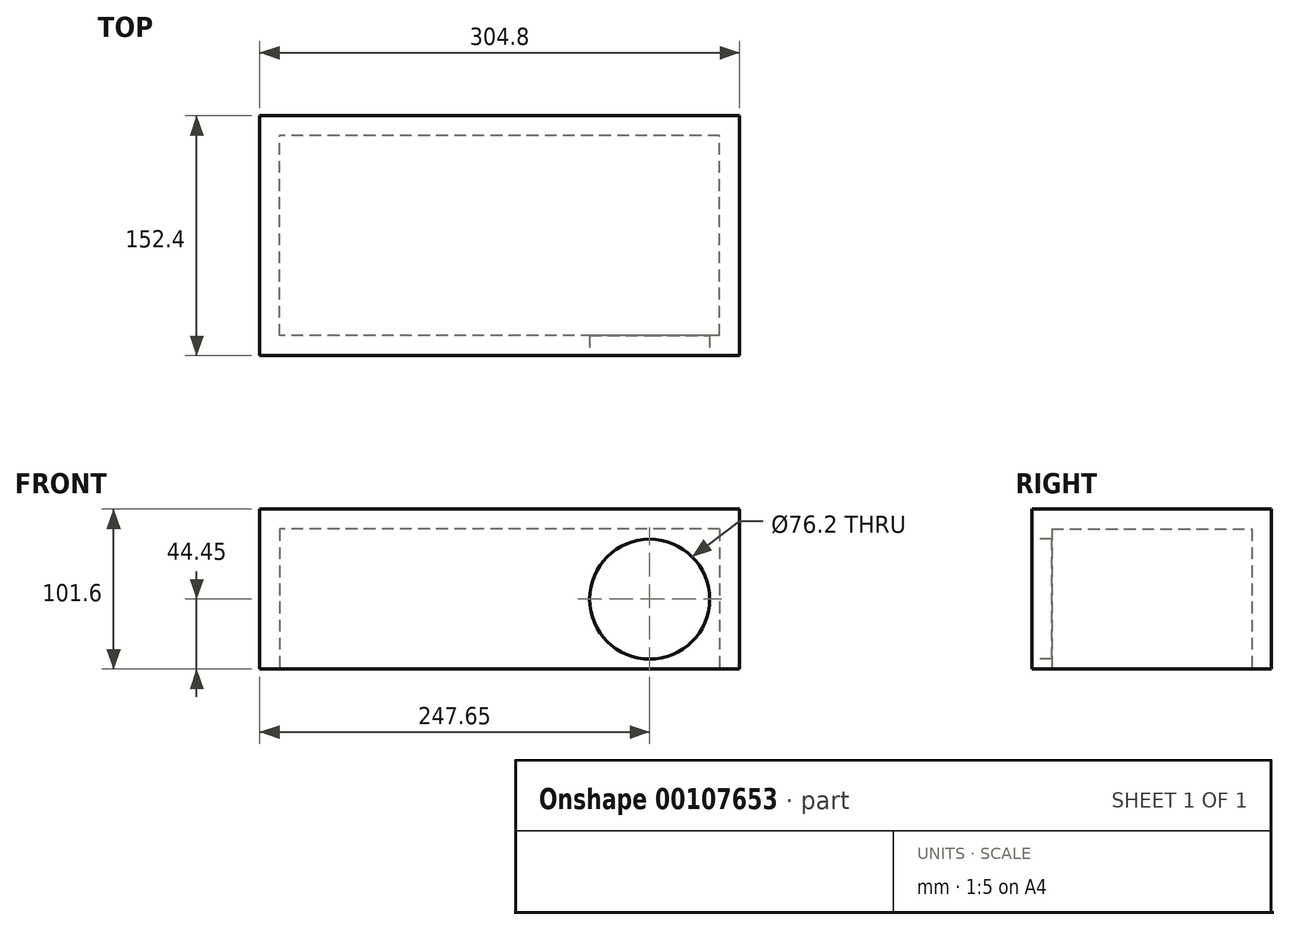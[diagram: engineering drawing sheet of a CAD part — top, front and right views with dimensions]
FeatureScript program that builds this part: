
annotation { "Feature Type Name" : "Feature", "Feature Type Description" : "" }
export const myFeature = defineFeature(function(context is Context, id is Id, definition is map)
    precondition{}
    {
        {
            var Q0;
            Q0=qCreatedBy(makeId("Front.planeOp"),FACE);
            var sketch = newSketch(context, id + "F0", { "sketchPlane" : qUnion([Q0])});
            skLineSegment(sketch, "E0.bottom", {"start": v(152.4, 50.8) * mm, "end": v(-152.4, 50.8) * mm});
            skLineSegment(sketch, "E0.top", {"start": v(152.4, -50.8) * mm, "end": v(-152.4, -50.8) * mm});
            skLineSegment(sketch, "E0.left", {"start": v(152.4, 50.8) * mm, "end": v(152.4, -50.8) * mm});
            skLineSegment(sketch, "E0.right", {"start": v(-152.4, 50.8) * mm, "end": v(-152.4, -50.8) * mm});
            skPoint(sketch, "E0.middle", {"position": v(0, 0) * mm});
            skSolve(sketch);
        }
        {
            var Q0;
            Q0 = qSketchRegion(id + "F0", true);
            extrude(context, id + "F1", {"entities" : qUnion([Q0]), "endBound" : BoundingType.SYMMETRIC, "depth" : 152.4 * mm});
        }
        {
            var Q0;
            Q0=makeQuery(id+"F1.opExtrude","SWEPT_FACE",FACE,{"disambiguationData":[OSD([sQuery(id+"F0.wireOp",EDGE,"E0.top")])]});
            var sketch = newSketch(context, id + "F2", { "sketchPlane" : qUnion([Q0])});
            skLineSegment(sketch, "E1.bottom", {"start": v(139.7, 63.5) * mm, "end": v(-139.7, 63.5) * mm});
            skLineSegment(sketch, "E1.top", {"start": v(139.7, -63.5) * mm, "end": v(-139.7, -63.5) * mm});
            skLineSegment(sketch, "E1.left", {"start": v(139.7, 63.5) * mm, "end": v(139.7, -63.5) * mm});
            skLineSegment(sketch, "E1.right", {"start": v(-139.7, 63.5) * mm, "end": v(-139.7, -63.5) * mm});
            skPoint(sketch, "E1.middle", {"position": v(0, 0) * mm});
            skSolve(sketch);
        }
        {
            var Q0;
            Q0 = qSketchRegion(id + "F2", true);
            extrude(context, id + "F3", {"entities" : qUnion([Q0]), "operationType" : NewBodyOperationType.REMOVE, "oppositeDirection" : true, "depth" : 88.9 * mm});
        }
        {
            var Q0;
            Q0=makeQuery(id+"F1.opExtrude","CAP_FACE",FACE,{"disambiguationData":[OSD([sQuery(id+"F0.wireOp",EDGE,"E0.bottom"),sQuery(id+"F0.wireOp",EDGE,"E0.top"),sQuery(id+"F0.wireOp",EDGE,"E0.left"),sQuery(id+"F0.wireOp",EDGE,"E0.right")])],"isStart":false});
            var sketch = newSketch(context, id + "F4", { "sketchPlane" : qUnion([Q0])});
            skLineSegment(sketch, "E2", {"start": v(152.4, 0) * mm, "end": v(101.6, 0) * mm, "construction": true});
            skLineSegment(sketch, "E3", {"start": v(101.6, 0) * mm, "end": v(95.25, 0) * mm, "construction": true});
            skLineSegment(sketch, "E4", {"start": v(95.25, 0) * mm, "end": v(95.25, -6.35) * mm, "construction": true});
            skCircle(sketch, "E5", {"center": v(95.25, -6.35) * mm, "radius": 38.1 * mm});
            skSolve(sketch);
        }
        {
            var Q0;
            Q0 = qSketchRegion(id + "F4", true);
            extrude(context, id + "F5", {"entities" : qUnion([Q0]), "operationType" : NewBodyOperationType.REMOVE, "oppositeDirection" : true, "depth" : 12.7 * mm});
        }
    });
